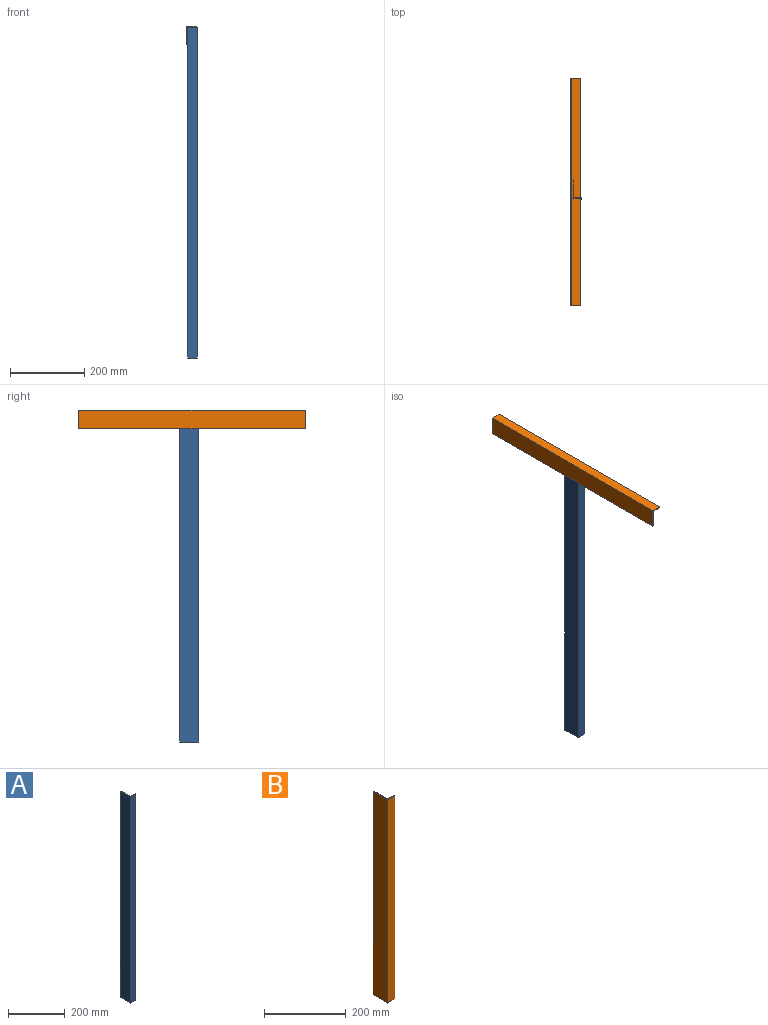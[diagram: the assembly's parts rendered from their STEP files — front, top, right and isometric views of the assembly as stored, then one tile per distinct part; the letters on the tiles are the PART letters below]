
ASSEMBLY  parts=2 mates=1
PART A: 8 faces, bbox 25.4x50.8x889 mm
  f0: plane 889x22.23mm, normal (0,1,0), area 19758mm2, adj f1,f5,f6,f7
  f1: plane 889x47.63mm, normal (1,0,0), area 42338.6mm2, adj f0,f2,f6,f7
  f2: plane 889x3.18mm, normal (0,1,0), area 2822.6mm2, adj f1,f3,f6,f7
  f3: plane 889x50.8mm, normal (-1,0,0), area 45161.2mm2, adj f2,f4,f6,f7
  f4: plane 889x25.4mm, normal (0,-1,0), area 22580.6mm2, adj f3,f5,f6,f7
  f5: plane 889x3.18mm, normal (1,0,0), area 2822.6mm2, adj f0,f4,f6,f7
  f6: plane 50.8x25.4mm, normal (0,0,1), area 231.9mm2, adj f0,f1,f2,f3,f4,f5
  f7: plane 50.8x25.4mm, normal (0,0,-1), area 231.9mm2, adj f0,f1,f2,f3,f4,f5
PART B: 8 faces, bbox 25.4x50.8x609.6 mm
  f0: plane 609.6x47.63mm, normal (1,0,0), area 29032.2mm2, adj f1,f5,f6,f7
  f1: plane 609.6x3.18mm, normal (0,1,0), area 1935.5mm2, adj f0,f2,f6,f7
  f2: plane 609.6x50.8mm, normal (-1,0,0), area 30967.7mm2, adj f1,f3,f6,f7
  f3: plane 609.6x25.4mm, normal (0,-1,0), area 15483.8mm2, adj f2,f4,f6,f7
  f4: plane 609.6x3.18mm, normal (1,0,0), area 1935.5mm2, adj f3,f5,f6,f7
  f5: plane 609.6x22.23mm, normal (0,1,0), area 13548.4mm2, adj f0,f4,f6,f7
  f6: plane 50.8x25.4mm, normal (0,0,1), area 231.9mm2, adj f0,f1,f2,f3,f4,f5
  f7: plane 50.8x25.4mm, normal (0,0,-1), area 231.9mm2, adj f0,f1,f2,f3,f4,f5
PLACE A t=(-244.12,36.09,83.05)mm
PLACE B rot(axis=(-1,0,0),90deg) t=(-247.3,-250.56,975.23)mm
MATE planar B.f0 <-> A.f3  axis (1,0,0) through (-244.12,54.24,948.24)mm
